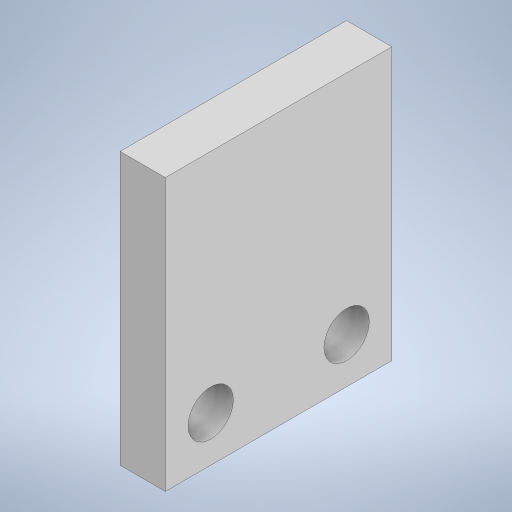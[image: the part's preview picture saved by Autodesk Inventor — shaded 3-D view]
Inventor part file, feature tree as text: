
AUTODESK INVENTOR PART (.ipt)
format: ipt  version: 2024.3 (Build 283343000, 343)  size: 260,096 bytes
history: native  units: mm
features: sketch x6, extrude x4, hole x2, other x1
ambient origin geometry x8: Origin, YZ Plane, XZ Plane, XY Plane, X Axis, Y Axis, Z Axis, Center Point
bodies: Body1 (feature_tree), Body2 (feature_tree)
feature tree (13):
  other  "ソリッド1"
  extrude  "押し出し1"  Depth=30.0mm
  hole  "穴1"  [1 undecoded]
  extrude  "押し出し2"  Depth=30.0mm
  hole  "穴2"  [1 undecoded]
  extrude  "押し出し3"  Depth=5.0mm TaperAngle=0.0deg
  extrude  "押し出し4"  Depth=10.0mm
  sketch  "スケッチ1"
  sketch  "スケッチ2"
  sketch  "スケッチ3"
  sketch  "スケッチ4"
  sketch  "スケッチ5"
  sketch  "スケッチ6"
note: 2 required parameter values undecoded (feature->parameter linkage not recoverable at this tier; creation-order binding heuristic only, values carry confidence <= 0.55)
